# Revit family: Showerhead-DXV-Traditional-D35700110_Series
name_source: partatom
category: Plumbing Fixtures
revit_build: Autodesk Revit 2014 (Build: 20130308_1515(x64)
units: mm (PartAtom-declared; Revit-internal decimal feet)

## types (3) — shared parameters
Assembly Code = D2010710
CW Connection = No
CWFU = 3
Default Elevation = 0"
Description = Traditional 10” Rain Showerhead
Flow Rate = 2.5 GPM (9.5L/min)
HW Connection = No
HWFU = 3
Height = 2 3/4"
Installation Type = Ceiling Mounted
Length = 10"
Manufacturer = DXV
Price = Prices may vary. Please consult Manufacturer Representative for most up-to-date price list.
Product Documentation Link = https://dxv01.blob.core.windows.net
Product Page URL = http://www.dxv.com
Revised Date = 03/10/2017
Tempered Water Connection = Yes
Tempered Water Connection Diameter = 1/2"
URL = www.dxv.com
Vent Connection = No
WFU = 4
Warranty Documentation Link = https://www.dxv.com
Waste Connection = No
Width = 10"

## per-type parameters (varying)
| type | ADA Compliant | Finish | Material |
| D35700110.150 | Yes | Metal-DXV-150-Platinum Nickel | Metal-DXV-150-Platinum Nickel |
| D35700110.100 | No | Metal-DXV-100-Polished Chrome | Metal-DXV-100-Polished Chrome |
| D35700110.144 | Yes | Metal-DXV-144-Brushed Nickel | Metal-DXV-144-Brushed Nickel |

note: column(s) folded — value = type name in every type: Model

## geometry (parser evidence)
native form markers: Sweep x1
no freeform markers — native parametric forms only
